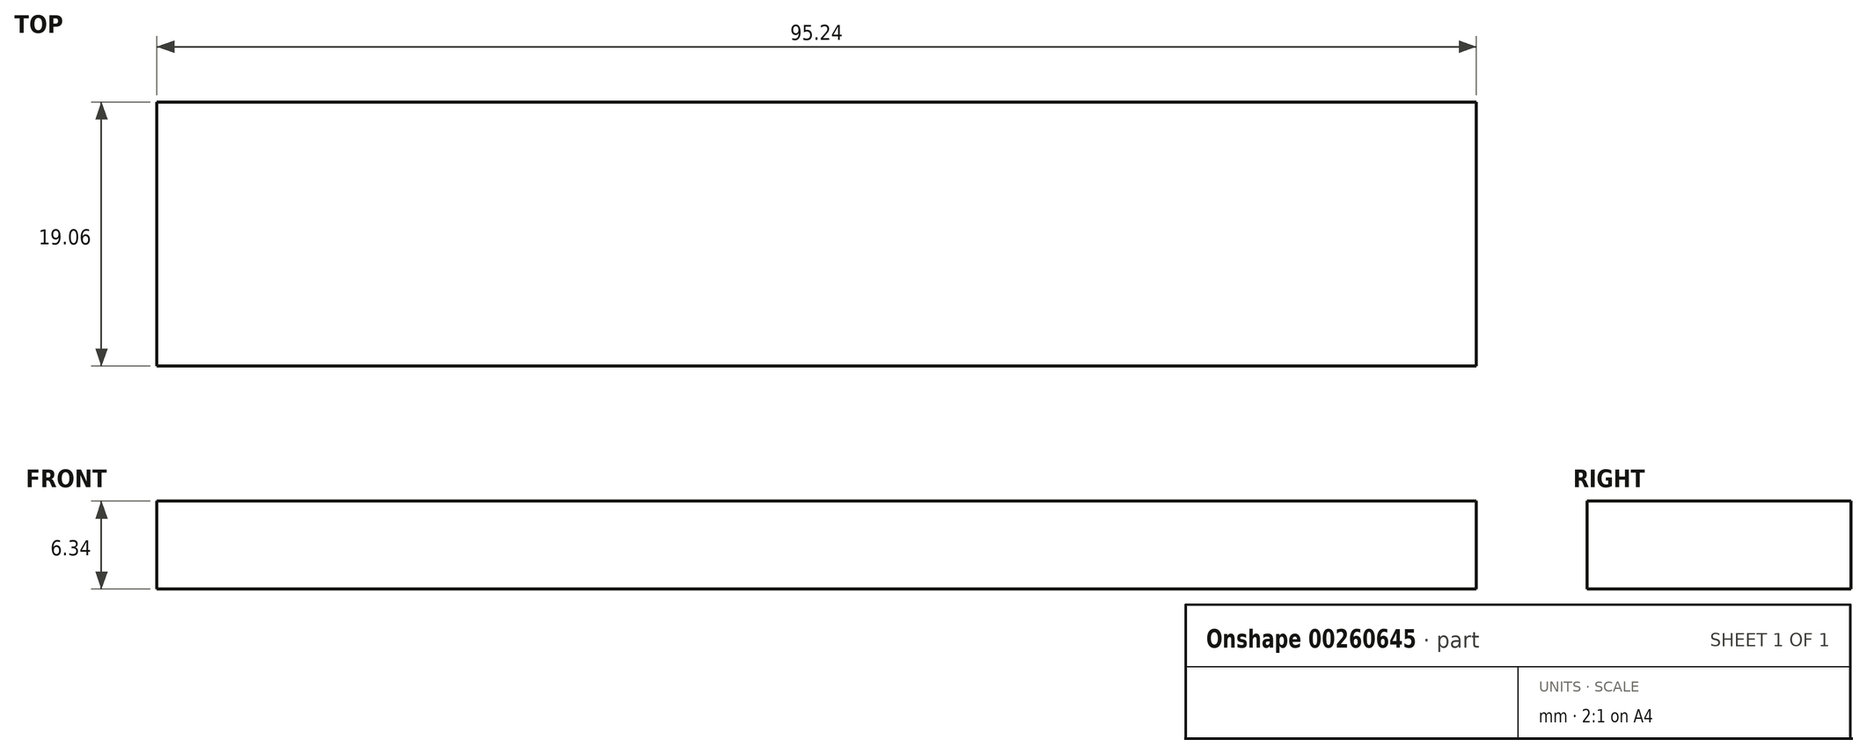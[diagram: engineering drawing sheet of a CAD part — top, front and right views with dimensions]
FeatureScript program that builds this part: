
annotation { "Feature Type Name" : "Feature", "Feature Type Description" : "" }
export const myFeature = defineFeature(function(context is Context, id is Id, definition is map)
    precondition{}
    {
        {
            var Q0;
            Q0=qCreatedBy(makeId("Top.planeOp"),FACE);
            var sketch = newSketch(context, id + "F0", { "sketchPlane" : qUnion([Q0])});
            skLineSegment(sketch, "E0.bottom", {"start": v(47.63, 9.53) * mm, "end": v(-47.63, 9.53) * mm});
            skLineSegment(sketch, "E0.top", {"start": v(47.63, -9.53) * mm, "end": v(-47.63, -9.53) * mm});
            skLineSegment(sketch, "E0.left", {"start": v(47.63, 9.53) * mm, "end": v(47.63, -9.53) * mm});
            skLineSegment(sketch, "E0.right", {"start": v(-47.63, 9.53) * mm, "end": v(-47.63, -9.53) * mm});
            skPoint(sketch, "E0.middle", {"position": v(0, 0) * mm});
            skSolve(sketch);
        }
        {
            var Q0;
            Q0 = qSketchRegion(id + "F0", true);
            extrude(context, id + "F1", {"entities" : qUnion([Q0]), "endBound" : BoundingType.SYMMETRIC, "depth" : 6.35 * mm});
        }
    });
